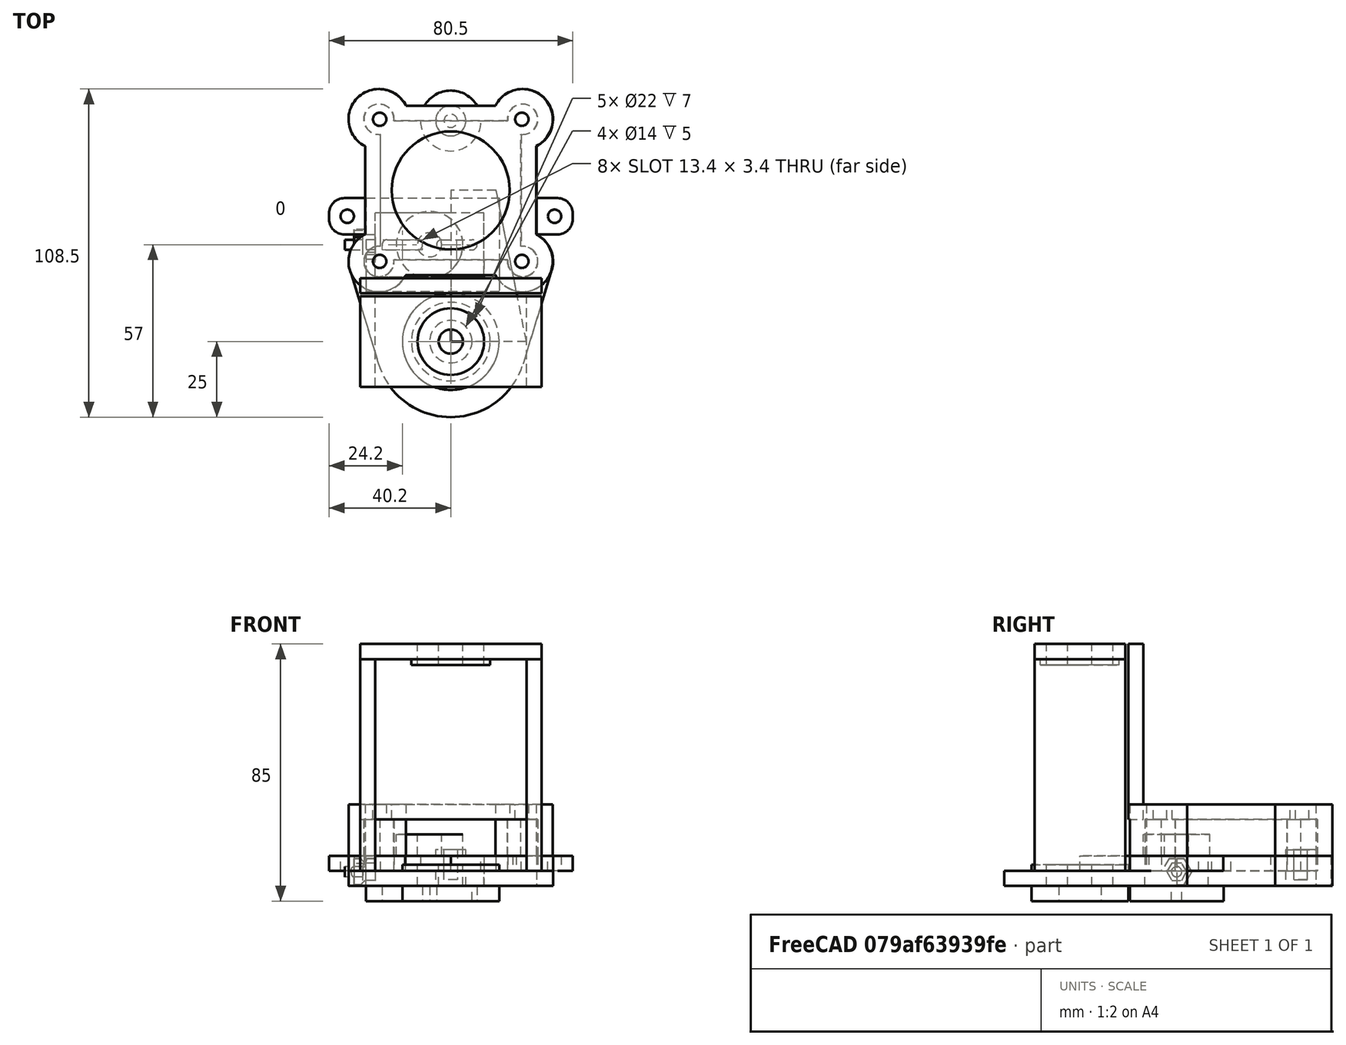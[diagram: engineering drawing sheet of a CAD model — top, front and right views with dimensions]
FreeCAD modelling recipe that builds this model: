
FCSTD DOCUMENT  (FreeCAD 0.16R6700 (Git))
Label: drive_full
License: All rights reserved
LicenseURL: http://en.wikipedia.org/wiki/All_rights_reserved
objects: Sketcher::SketchObject×23, PartDesign::Pocket×12, Part::Cylinder×8, PartDesign::Pad×8, Part::MultiFuse×5, Part::Cut×4, Part::Box×4, Mesh::Feature×3, Part::Extrusion×3, Part::Thickness×3, App::DocumentObjectGroup×1
note: 90 computed .brp shape members not serialized (recipe doc carries the construction recipe); baked Part::Feature solids carry a one-line shape summary decoded from their .brp

FEATURE [Mesh::Feature] pulley_full
  Placement = pos=(0,0,-3) rot=(0,0,1;0rad)
FEATURE [Part::Cylinder] Cylinder
  Angle = 360
  Height = 7
  Radius = 11
FEATURE [Part::Cylinder] Cylinder001
  Angle = 360
  Height = 7
  Radius = 4
FEATURE [Part::Cut] Cut  label="608"
  Base = -> Cylinder
  Placement = pos=(0,0,61) rot=(0,0,1;0rad)
  Tool = -> Cylinder001
FEATURE [Part::Cylinder] Cylinder002
  Angle = 360
  Height = 7
  Radius = 11
FEATURE [Part::Cylinder] Cylinder003
  Angle = 360
  Height = 7
  Radius = 4
FEATURE [Part::Cut] Cut001  label="608-1"
  Base = -> Cylinder002
  Placement = pos=(0,0,-12) rot=(0,0,1;0rad)
  Tool = -> Cylinder003
FEATURE [Mesh::Feature] nema23_76  label="nema23-76"
  Placement = pos=(0,50,14) rot=(0,0,1;0rad)
FEATURE [Part::Cylinder] Cylinder004
  Angle = 360
  Height = 7
  Radius = 11
FEATURE [Part::Cylinder] Cylinder005
  Angle = 360
  Height = 7
  Radius = 4
FEATURE [Part::Cut] Cut002  label="608-3"
  Base = -> Cylinder004
  Placement = pos=(-7,32,-2) rot=(0,0,1;0rad)
  Tool = -> Cylinder005
FEATURE [Part::Box] Box001  label="motor_wall"
  Height = 58
  Length = 60
  Placement = pos=(-30,16,10) rot=(0,0,1;0rad)
  Width = 5
FEATURE [Part::Box] Box002  label="rear_bearing_wall"
  Height = 5
  Length = 60
  Placement = pos=(-30,-15,66) rot=(0,0,1;0rad)
  Width = 30
FEATURE [Part::Cylinder] Cylinder012  label="rear_bearing_support"
  Angle = 360
  Height = 7
  Placement = pos=(0,0,64) rot=(0,0,1;0rad)
  Radius = 13
FEATURE [Part::Cylinder] Cylinder013  label="rear_bearing_hole"
  Angle = 360
  Height = 7
  Placement = pos=(0,0,64) rot=(0,0,1;0rad)
  Radius = 11
FEATURE [Part::MultiFuse] Fusion
  Shapes = -> [Cylinder012,Box002]
FEATURE [Part::Cut] Cut009  label="rear_pulley_wall"
  Base = -> Fusion
  Placement = pos=(0,0,-3) rot=(0,0,1;0rad)
  Tool = -> Cylinder013
FEATURE [Part::Box] Box004  label="side_wall"
  Height = 70
  Length = 5
  Placement = pos=(25,-15,-7) rot=(0,0,1;0rad)
  Width = 30
FEATURE [Part::Box] Box005  label="side_wall2"
  Height = 70
  Length = 5
  Placement = pos=(-30,-15,-7) rot=(0,0,1;0rad)
  Width = 30
FEATURE [App::DocumentObjectGroup] Group
FEATURE [Sketcher::SketchObject] Sketch002
  Placement = pos=(-30,-16,-12) rot=(0,0,1;0rad)
  sketch-geometry (7):
    g0: LineSegment StartX=2 StartY=63.5 StartZ=0 EndX=46 EndY=63.5 EndZ=0
    g1: LineSegment StartX=46 StartY=63.5 StartZ=0 EndX=46 EndY=32.5 EndZ=0
    g2: LineSegment StartX=46 StartY=32.5 StartZ=0 EndX=2 EndY=32.5 EndZ=0
    g3: LineSegment StartX=2 StartY=63.5 StartZ=0 EndX=2 EndY=32.5 EndZ=0
    g4: GeomPoint [constr] X=0 Y=52.9218 Z=0
    g5: GeomPoint [constr] X=2 Y=63.5 Z=0
    g6: GeomPoint [constr] X=8.31916 Y=32.5 Z=0
  constraints (15):
    c: Horizontal(g0)
    c: Vertical(g1)
    c: Horizontal(g2)
    c: Vertical(g3)
    c: Coincident(g0,g3)
    c: Coincident(g0,g1)
    c: Coincident(g1,g2)
    c: Coincident(g2,g3)
    c: DistanceY(g1,g1) = 31
    c: Distance(g2) = 44
    c: PointOnObject(g4,g-2)
    c: Coincident(g0,g5)
    c: DistanceX(g4,g5) = 2
    c: PointOnObject(g6,g2)
    c: DistanceY(g-1,g6) = 32.5
FEATURE [PartDesign::Pad] Pad  label="tuner_roof"
  Length = 5
  Length2 = 100
  Placement = pos=(-30,-16,-12) rot=(0,0,1;0rad)
  Reversed = true
  Sketch = -> Sketch002
  Type = 0
FEATURE [Sketcher::SketchObject] Sketch003
  ExternalGeometry = -> [Pad]
  Placement = pos=(-30,-16,-17) rot=(1,0,0;3.14159rad)
  Support = -> Pad [Face6]
  sketch-geometry (10):
    g0: ArcOfCircle CenterX=9 CenterY=-48 CenterZ=0 NormalX=0 NormalY=0 NormalZ=1 Radius=1.7 StartAngle=1.5708 EndAngle=4.71239
    g1: ArcOfCircle CenterX=19 CenterY=-48 CenterZ=0 NormalX=0 NormalY=0 NormalZ=1 Radius=1.7 StartAngle=4.71239 EndAngle=7.85398
    g2: LineSegment StartX=9 StartY=-49.7 StartZ=0 EndX=19 EndY=-49.7 EndZ=0
    g3: LineSegment StartX=9 StartY=-46.3 StartZ=0 EndX=19 EndY=-46.3 EndZ=0
    g4: ArcOfCircle CenterX=27 CenterY=-48 CenterZ=0 NormalX=0 NormalY=0 NormalZ=1 Radius=1.7 StartAngle=1.5708 EndAngle=4.71239
    g5: ArcOfCircle CenterX=37 CenterY=-48 CenterZ=0 NormalX=0 NormalY=0 NormalZ=1 Radius=1.7 StartAngle=4.71239 EndAngle=7.85398
    g6: LineSegment StartX=27 StartY=-49.7 StartZ=0 EndX=37 EndY=-49.7 EndZ=0
    g7: LineSegment StartX=27 StartY=-46.3 StartZ=0 EndX=37 EndY=-46.3 EndZ=0
    g8: GeomPoint [constr] X=6.41583 Y=-32.5 Z=0
    g9: GeomPoint [constr] X=0 Y=-49.7364 Z=0
  constraints (22):
    c: Tangent(g0,g3) = 1.5708
    c: Tangent(g0,g2) = -1.5708
    c: Tangent(g2,g1) = -1.5708
    c: Tangent(g3,g1) = 1.5708
    c: Horizontal(g2)
    c: Equal(g0,g1)
    c: Tangent(g4,g7) = 1.5708
    c: Tangent(g4,g6) = -1.5708
    c: Tangent(g6,g5) = -1.5708
    c: Tangent(g7,g5) = 1.5708
    c: Horizontal(g6)
    c: Equal(g4,g5)
    c: DistanceY(g0,g4) = 0
    c: Radius(g1) = 1.7
    c: Radius(g4) = 1.7
    c: PointOnObject(g8,g-3)
    c: DistanceY(g0,g8) = 15.5
    c: Distance(g1,g0) = 10
    c: Distance(g4,g5) = 10
    c: Distance(g5,g1) = 18
    c: PointOnObject(g9,g-2)
    c: DistanceX(g9,g0) = 9
FEATURE [PartDesign::Pocket] Pocket001  label="tune_bolts_cut"
  Length = 5
  Placement = pos=(-30,-16,-12) rot=(0,0,1;0rad)
  Sketch = -> Sketch003
  Type = 0
FEATURE [Mesh::Feature] bearing_holder
  Placement = pos=(-7,32,-12) rot=(0,0,1;3.14159rad)
FEATURE [Sketcher::SketchObject] Sketch006
  Placement = pos=(0,0,-2) rot=(0,0,1;0rad)
  sketch-geometry (21):
    g0: LineSegment StartX=-18.8251 StartY=27 StartZ=0 EndX=18.7251 EndY=27 EndZ=0
    g1: LineSegment StartX=23.2 StartY=31.4749 StartZ=0 EndX=23.2 EndY=68.5251 EndZ=0
    g2: LineSegment StartX=18.7251 StartY=73 StartZ=0 EndX=-18.8251 EndY=73 EndZ=0
    g3: LineSegment StartX=-23.3 StartY=68.5251 StartZ=0 EndX=-23.3 EndY=31.4749 EndZ=0
    g4: GeomPoint [constr] X=23.2 Y=67.9149 Z=0
    g5: GeomPoint [constr] X=18.0919 Y=73 Z=0
    g6: GeomPoint [constr] X=-23.3 Y=67.7035 Z=0
    g7: GeomPoint [constr] X=-23.3 Y=27 Z=0
    g8: GeomPoint [constr] X=23.2 Y=67.7619 Z=0
    g9: ArcOfCircle CenterX=-23.8 CenterY=26.5 CenterZ=0 NormalX=0 NormalY=0 NormalZ=1 Radius=5 StartAngle=1.47063 EndAngle=6.38335
    g10: GeomPoint [constr] X=-23.3 Y=27 Z=0
    g11: ArcOfCircle CenterX=23.7 CenterY=26.5 CenterZ=0 NormalX=0 NormalY=0 NormalZ=1 Radius=5 StartAngle=3.04143 EndAngle=7.95415
    g12: GeomPoint [constr] X=23.2 Y=27 Z=0
    g13: GeomPoint [constr] X=23.2 Y=27 Z=0
    g14: ArcOfCircle CenterX=23.7 CenterY=73.5 CenterZ=0 NormalX=0 NormalY=0 NormalZ=1 Radius=5 StartAngle=4.61222 EndAngle=9.52495
    g15: GeomPoint [constr] X=23.2 Y=66.2729 Z=0
    g16: ArcOfCircle CenterX=-23.8 CenterY=73.5 CenterZ=0 NormalX=0 NormalY=0 NormalZ=1 Radius=5 StartAngle=6.18302 EndAngle=11.0957
    g17: GeomPoint [constr] X=-9.4334 Y=27 Z=0
    g18: GeomPoint [constr] X=-8.84955 Y=0 Z=0
    g19: GeomPoint [constr] X=0 Y=23.7268 Z=0
    g20: GeomPoint [constr] X=23.2 Y=34.2071 Z=0
  constraints (43):
    c: Horizontal(g0)
    c: Horizontal(g2)
    c: Vertical(g1)
    c: Vertical(g3)
    c: PointOnObject(g4,g1)
    c: PointOnObject(g5,g2)
    c: PointOnObject(g6,g3)
    c: PointOnObject(g7,g0)
    c: DistanceY(g7,g5) = 46
    c: PointOnObject(g8,g1)
    c: DistanceX(g6,g8) = 46.5
    c: Radius(g9) = 5
    c: DistanceY(g9,g7) = 0.5
    c: PointOnObject(g10,g3)
    c: DistanceX(g9,g10) = 0.5
    c: Equal(g9,g11) = 5
    c: PointOnObject(g13,g1)
    c: DistanceY(g11,g12) = 0.5
    c: PointOnObject(g12,g0)
    c: DistanceX(g13,g11) = 0.5
    c: Coincident(g12,g13)
    c: Coincident(g7,g10)
    c: DistanceY(g5,g14) = 0.5
    c: PointOnObject(g15,g1)
    c: DistanceX(g15,g14) = 0.5
    c: DistanceX(g16,g6) = 0.5
    c: DistanceY(g5,g16) = 0.5
    c: Equal(g14,g16)
    c: Coincident(g2,g16)
    c: Coincident(g3,g16)
    c: Equal(g11,g14)
    c: Coincident(g1,g14)
    c: Coincident(g2,g14)
    c: Coincident(g11,g0)
    c: Coincident(g11,g1)
    c: Coincident(g0,g9)
    c: Coincident(g3,g9)
    c: PointOnObject(g17,g0)
    c: PointOnObject(g18,g-1)
    c: DistanceY(g18,g17) = 27
    c: PointOnObject(g19,g-2)
    c: PointOnObject(g20,g1)
    c: DistanceX(g19,g20) = 23.2
FEATURE [Part::Extrusion] Extrude
  Base = -> Sketch006
  Dir = (0,0,12)
  Solid = true
FEATURE [Part::Thickness] Thickness  label="curved_walls"
  Faces = -> Extrude [Face9]
  Intersection = false
  Join = 2
  Mode = 0
  SelfIntersection = false
  Value = 5
FEATURE [Sketcher::SketchObject] Sketch007
  Placement = pos=(0,0,15) rot=(0,0,1;0rad)
  Support = -> Thickness [Face19]
  sketch-geometry (7):
    g0: Circle CenterX=-23.5 CenterY=73.5 CenterZ=0 NormalX=0 NormalY=0 NormalZ=1 Radius=2.2
    g1: GeomPoint [constr] X=0 Y=49.9672 Z=0
    g2: GeomPoint [constr] X=-26.4919 Y=0 Z=0
    g3: Circle CenterX=-23.5 CenterY=26.5 CenterZ=0 NormalX=0 NormalY=0 NormalZ=1 Radius=2.2
    g4: Circle CenterX=23.5 CenterY=26.5 CenterZ=0 NormalX=0 NormalY=0 NormalZ=1 Radius=2.2
    g5: Circle CenterX=23.5 CenterY=73.5 CenterZ=0 NormalX=0 NormalY=0 NormalZ=1 Radius=2.2
    g6: Circle CenterX=0 CenterY=50 CenterZ=0 NormalX=0 NormalY=0 NormalZ=1 Radius=19.5
  constraints (17):
    c: Radius(g0) = 2.2
    c: PointOnObject(g1,g-2)
    c: DistanceX(g0,g1) = 23.5
    c: PointOnObject(g2,g-1)
    c: DistanceY(g2,g0) = 73.5
    c: Equal(g0,g3) = 2.2
    c: Equal(g3,g4)
    c: Equal(g5,g4)
    c: DistanceX(g3,g1) = 23.5
    c: DistanceX(g1,g5) = 23.5
    c: DistanceX(g1,g4) = 23.5
    c: DistanceY(g2,g5) = 73.5
    c: DistanceY(g2,g4) = 26.5
    c: DistanceY(g2,g3) = 26.5
    c: PointOnObject(g6,g-2)
    c: Radius(g6) = 19.5
    c: DistanceY(g2,g6) = 50
FEATURE [PartDesign::Pocket] Pocket003  label="bolt_holes"
  Length = 5
  Sketch = -> Sketch007
  Type = 0
FEATURE [Sketcher::SketchObject] Sketch008
  Placement = pos=(0,0,-7) rot=(0,0,1;0rad)
  sketch-geometry (21):
    g0: LineSegment StartX=-18.8251 StartY=27 StartZ=0 EndX=18.7251 EndY=27 EndZ=0
    g1: LineSegment StartX=23.2 StartY=31.4749 StartZ=0 EndX=23.2 EndY=68.5251 EndZ=0
    g2: LineSegment StartX=18.7251 StartY=73 StartZ=0 EndX=-18.8251 EndY=73 EndZ=0
    g3: LineSegment StartX=-23.3 StartY=68.5251 StartZ=0 EndX=-23.3 EndY=31.4749 EndZ=0
    g4: GeomPoint [constr] X=23.2 Y=67.9149 Z=0
    g5: GeomPoint [constr] X=18.0919 Y=73 Z=0
    g6: GeomPoint [constr] X=-23.3 Y=67.7035 Z=0
    g7: GeomPoint [constr] X=-23.3 Y=27 Z=0
    g8: GeomPoint [constr] X=23.2 Y=67.7619 Z=0
    g9: ArcOfCircle CenterX=-23.8 CenterY=26.5 CenterZ=0 NormalX=0 NormalY=0 NormalZ=1 Radius=5 StartAngle=1.47063 EndAngle=6.38335
    g10: GeomPoint [constr] X=-23.3 Y=27 Z=0
    g11: ArcOfCircle CenterX=23.7 CenterY=26.5 CenterZ=0 NormalX=0 NormalY=0 NormalZ=1 Radius=5 StartAngle=3.04143 EndAngle=7.95415
    g12: GeomPoint [constr] X=23.2 Y=27 Z=0
    g13: GeomPoint [constr] X=23.2 Y=27 Z=0
    g14: ArcOfCircle CenterX=23.7 CenterY=73.5 CenterZ=0 NormalX=0 NormalY=0 NormalZ=1 Radius=5 StartAngle=4.61222 EndAngle=9.52495
    g15: GeomPoint [constr] X=23.2 Y=66.2729 Z=0
    g16: ArcOfCircle CenterX=-23.8 CenterY=73.5 CenterZ=0 NormalX=0 NormalY=0 NormalZ=1 Radius=5 StartAngle=6.18302 EndAngle=11.0957
    g17: GeomPoint [constr] X=-9.4334 Y=27 Z=0
    g18: GeomPoint [constr] X=-8.84955 Y=0 Z=0
    g19: GeomPoint [constr] X=0 Y=23.7268 Z=0
    g20: GeomPoint [constr] X=23.2 Y=34.2071 Z=0
  constraints (43):
    c: Horizontal(g0)
    c: Horizontal(g2)
    c: Vertical(g1)
    c: Vertical(g3)
    c: PointOnObject(g4,g1)
    c: PointOnObject(g5,g2)
    c: PointOnObject(g6,g3)
    c: PointOnObject(g7,g0)
    c: DistanceY(g7,g5) = 46
    c: PointOnObject(g8,g1)
    c: DistanceX(g6,g8) = 46.5
    c: Radius(g9) = 5
    c: DistanceY(g9,g7) = 0.5
    c: PointOnObject(g10,g3)
    c: DistanceX(g9,g10) = 0.5
    c: Equal(g9,g11) = 5
    c: PointOnObject(g13,g1)
    c: DistanceY(g11,g12) = 0.5
    c: PointOnObject(g12,g0)
    c: DistanceX(g13,g11) = 0.5
    c: Coincident(g12,g13)
    c: Coincident(g7,g10)
    c: DistanceY(g5,g14) = 0.5
    c: PointOnObject(g15,g1)
    c: DistanceX(g15,g14) = 0.5
    c: DistanceX(g16,g6) = 0.5
    c: DistanceY(g5,g16) = 0.5
    c: Equal(g14,g16)
    c: Coincident(g2,g16)
    c: Coincident(g3,g16)
    c: Equal(g11,g14)
    c: Coincident(g1,g14)
    c: Coincident(g2,g14)
    c: Coincident(g11,g0)
    c: Coincident(g11,g1)
    c: Coincident(g0,g9)
    c: Coincident(g3,g9)
    c: PointOnObject(g17,g0)
    c: PointOnObject(g18,g-1)
    c: DistanceY(g18,g17) = 27
    c: PointOnObject(g19,g-2)
    c: PointOnObject(g20,g1)
    c: DistanceX(g19,g20) = 23.2
FEATURE [Part::Extrusion] Extrude001
  Base = -> Sketch008
  Dir = (0,0,-5)
  Solid = true
FEATURE [Part::Thickness] Thickness001  label="roof"
  Faces = -> Extrude001 [Face10]
  Intersection = false
  Join = 2
  Mode = 2
  Placement = pos=(0,0,-14) rot=(0,1,0;3.14159rad)
  SelfIntersection = false
  Value = 5
FEATURE [Sketcher::SketchObject] Sketch009
  ExternalGeometry = -> [Thickness001]
  Placement = pos=(0,0,-12) rot=(0,1,0;3.14159rad)
  Support = -> Thickness001 [Face19]
  sketch-geometry (6):
    g0: LineSegment StartX=-33.3619 StartY=23.5727 StartZ=0 EndX=-23.9049 EndY=-7.31832 EndZ=0
    g1: LineSegment StartX=33.2706 StartY=23.601 StartZ=0 EndX=23.9264 EndY=-7.24743 EndZ=0
    g2: LineSegment StartX=-23.8 StartY=26.5 StartZ=0 EndX=-33.3619 EndY=23.5727 EndZ=0
    g3: LineSegment StartX=23.7 StartY=26.5 StartZ=0 EndX=33.2706 EndY=23.601 EndZ=0
    g4: LineSegment StartX=-23.8 StartY=26.5 StartZ=0 EndX=23.7 EndY=26.5 EndZ=0
    g5: ArcOfCircle CenterX=0 CenterY=0 CenterZ=0 NormalX=0 NormalY=0 NormalZ=1 Radius=25 StartAngle=3.43868 EndAngle=5.98907
  constraints (14):
    c: PointOnObject(g0,g-3)
    c: Coincident(g2,g-3)
    c: Coincident(g2,g0)
    c: Perpendicular(g0,g2)
    c: Coincident(g3,g1)
    c: Perpendicular(g3,g1)
    c: Coincident(g4,g2)
    c: Tangent(g0,g5) = -1.5708
    c: Tangent(g1,g5) = 1.5708
    c: Radius(g5) = 25
    c: Coincident(g-1,g5)
    c: Coincident(g3,g4)
    c: Coincident(g3,g-4)
    c: PointOnObject(g1,g-4)
FEATURE [PartDesign::Pad] Pad001
  Length = 5
  Length2 = 100
  Placement = pos=(0,0,-14) rot=(0,1,0;3.14159rad)
  Reversed = true
  Sketch = -> Sketch009
  Type = 0
FEATURE [Part::MultiFuse] Fusion001  label="roof_full"
  Shapes = -> [Pad001,Thickness001]
FEATURE [Sketcher::SketchObject] Sketch010
  Placement = pos=(0,0,-12) rot=(1,0,0;3.14159rad)
  Support = -> Fusion001 [Face12]
  sketch-geometry (7):
    g0: LineSegment StartX=-25 StartY=-21.5 StartZ=0 EndX=11 EndY=-21.5 EndZ=0
    g1: LineSegment StartX=11 StartY=-21.5 StartZ=0 EndX=11 EndY=-42.5 EndZ=0
    g2: LineSegment StartX=11 StartY=-42.5 StartZ=0 EndX=-25 EndY=-42.5 EndZ=0
    g3: LineSegment StartX=-25 StartY=-21.5 StartZ=0 EndX=-25 EndY=-42.5 EndZ=0
    g4: GeomPoint [constr] X=0 Y=52.9218 Z=0
    g5: GeomPoint [constr] X=-25 Y=-21.5 Z=0
    g6: GeomPoint [constr] X=8.31916 Y=-42.5 Z=0
  constraints (15):
    c: Horizontal(g0)
    c: Vertical(g1)
    c: Horizontal(g2)
    c: Vertical(g3)
    c: Coincident(g0,g3)
    c: Coincident(g0,g1)
    c: Coincident(g1,g2)
    c: Coincident(g2,g3)
    c: DistanceY(g1,g1) = 21
    c: Distance(g2) = 36
    c: PointOnObject(g4,g-2)
    c: Coincident(g0,g5)
    c: DistanceX(g4,g5) = -25
    c: PointOnObject(g6,g2)
    c: DistanceY(g-1,g6) = -42.5
FEATURE [PartDesign::Pocket] Pocket
  Length = 10
  Sketch = -> Sketch010
  Type = 0
FEATURE [Sketcher::SketchObject] Sketch012
  Placement = pos=(0,0,-7) rot=(0,0,1;0rad)
  sketch-geometry (21):
    g0: LineSegment StartX=-18.8251 StartY=27 StartZ=0 EndX=18.7251 EndY=27 EndZ=0
    g1: LineSegment StartX=23.2 StartY=31.4749 StartZ=0 EndX=23.2 EndY=68.5251 EndZ=0
    g2: LineSegment StartX=18.7251 StartY=73 StartZ=0 EndX=-18.8251 EndY=73 EndZ=0
    g3: LineSegment StartX=-23.3 StartY=68.5251 StartZ=0 EndX=-23.3 EndY=31.4749 EndZ=0
    g4: GeomPoint [constr] X=23.2 Y=67.9149 Z=0
    g5: GeomPoint [constr] X=18.0919 Y=73 Z=0
    g6: GeomPoint [constr] X=-23.3 Y=67.7035 Z=0
    g7: GeomPoint [constr] X=-23.3 Y=27 Z=0
    g8: GeomPoint [constr] X=23.2 Y=67.7619 Z=0
    g9: ArcOfCircle CenterX=-23.8 CenterY=26.5 CenterZ=0 NormalX=0 NormalY=0 NormalZ=1 Radius=5 StartAngle=1.47063 EndAngle=6.38335
    g10: GeomPoint [constr] X=-23.3 Y=27 Z=0
    g11: ArcOfCircle CenterX=23.7 CenterY=26.5 CenterZ=0 NormalX=0 NormalY=0 NormalZ=1 Radius=5 StartAngle=3.04143 EndAngle=7.95415
    g12: GeomPoint [constr] X=23.2 Y=27 Z=0
    g13: GeomPoint [constr] X=23.2 Y=27 Z=0
    g14: ArcOfCircle CenterX=23.7 CenterY=73.5 CenterZ=0 NormalX=0 NormalY=0 NormalZ=1 Radius=5 StartAngle=4.61222 EndAngle=9.52495
    g15: GeomPoint [constr] X=23.2 Y=66.2729 Z=0
    g16: ArcOfCircle CenterX=-23.8 CenterY=73.5 CenterZ=0 NormalX=0 NormalY=0 NormalZ=1 Radius=5 StartAngle=6.18302 EndAngle=11.0957
    g17: GeomPoint [constr] X=-9.4334 Y=27 Z=0
    g18: GeomPoint [constr] X=-8.84955 Y=0 Z=0
    g19: GeomPoint [constr] X=0 Y=23.7268 Z=0
    g20: GeomPoint [constr] X=23.2 Y=34.2071 Z=0
  constraints (43):
    c: Horizontal(g0)
    c: Horizontal(g2)
    c: Vertical(g1)
    c: Vertical(g3)
    c: PointOnObject(g4,g1)
    c: PointOnObject(g5,g2)
    c: PointOnObject(g6,g3)
    c: PointOnObject(g7,g0)
    c: DistanceY(g7,g5) = 46
    c: PointOnObject(g8,g1)
    c: DistanceX(g6,g8) = 46.5
    c: Radius(g9) = 5
    c: DistanceY(g9,g7) = 0.5
    c: PointOnObject(g10,g3)
    c: DistanceX(g9,g10) = 0.5
    c: Equal(g9,g11) = 5
    c: PointOnObject(g13,g1)
    c: DistanceY(g11,g12) = 0.5
    c: PointOnObject(g12,g0)
    c: DistanceX(g13,g11) = 0.5
    c: Coincident(g12,g13)
    c: Coincident(g7,g10)
    c: DistanceY(g5,g14) = 0.5
    c: PointOnObject(g15,g1)
    c: DistanceX(g15,g14) = 0.5
    c: DistanceX(g16,g6) = 0.5
    c: DistanceY(g5,g16) = 0.5
    c: Equal(g14,g16)
    c: Coincident(g2,g16)
    c: Coincident(g3,g16)
    c: Equal(g11,g14)
    c: Coincident(g1,g14)
    c: Coincident(g2,g14)
    c: Coincident(g11,g0)
    c: Coincident(g11,g1)
    c: Coincident(g0,g9)
    c: Coincident(g3,g9)
    c: PointOnObject(g17,g0)
    c: PointOnObject(g18,g-1)
    c: DistanceY(g18,g17) = 27
    c: PointOnObject(g19,g-2)
    c: PointOnObject(g20,g1)
    c: DistanceX(g19,g20) = 23.2
FEATURE [Part::Extrusion] Extrude002
  Base = -> Sketch012
  Dir = (0,0,-5)
  Solid = true
FEATURE [Part::Thickness] Thickness002  label="roof001"
  Faces = -> Extrude002 [Face10]
  Intersection = false
  Join = 2
  Mode = 2
  Placement = pos=(0,0,-14) rot=(0,1,0;3.14159rad)
  SelfIntersection = false
  Value = 5
FEATURE [Sketcher::SketchObject] Sketch013
  ExternalGeometry = -> [Thickness002]
  Placement = pos=(0,0,-12) rot=(0,1,0;3.14159rad)
  Support = -> Thickness002 [Face19]
  sketch-geometry (6):
    g0: LineSegment StartX=-33.3619 StartY=23.5727 StartZ=0 EndX=-23.9049 EndY=-7.31832 EndZ=0
    g1: LineSegment StartX=33.2706 StartY=23.601 StartZ=0 EndX=23.9264 EndY=-7.24743 EndZ=0
    g2: LineSegment StartX=-23.8 StartY=26.5 StartZ=0 EndX=-33.3619 EndY=23.5727 EndZ=0
    g3: LineSegment StartX=23.7 StartY=26.5 StartZ=0 EndX=33.2706 EndY=23.601 EndZ=0
    g4: LineSegment StartX=-23.8 StartY=26.5 StartZ=0 EndX=23.7 EndY=26.5 EndZ=0
    g5: ArcOfCircle CenterX=0 CenterY=0 CenterZ=0 NormalX=0 NormalY=0 NormalZ=1 Radius=25 StartAngle=3.43868 EndAngle=5.98907
  constraints (14):
    c: PointOnObject(g0,g-3)
    c: Coincident(g2,g-3)
    c: Coincident(g2,g0)
    c: Perpendicular(g0,g2)
    c: Coincident(g3,g1)
    c: Perpendicular(g3,g1)
    c: Coincident(g4,g2)
    c: Tangent(g0,g5) = -1.5708
    c: Tangent(g1,g5) = 1.5708
    c: Radius(g5) = 25
    c: Coincident(g-1,g5)
    c: Coincident(g3,g4)
    c: Coincident(g3,g-4)
    c: PointOnObject(g1,g-4)
FEATURE [PartDesign::Pad] Pad002
  Length = 5
  Length2 = 100
  Placement = pos=(0,0,-14) rot=(0,1,0;3.14159rad)
  Reversed = true
  Sketch = -> Sketch013
  Type = 0
FEATURE [Part::MultiFuse] Fusion002  label="roof_full001"
  Shapes = -> [Pad002,Thickness002]
FEATURE [Sketcher::SketchObject] Sketch014
  Placement = pos=(0,0,-12) rot=(1,0,0;3.14159rad)
  Support = -> Fusion002 [Face12]
  sketch-geometry (7):
    g0: LineSegment StartX=-25 StartY=-21.5 StartZ=0 EndX=11 EndY=-21.5 EndZ=0
    g1: LineSegment StartX=11 StartY=-21.5 StartZ=0 EndX=11 EndY=-42.5 EndZ=0
    g2: LineSegment StartX=11 StartY=-42.5 StartZ=0 EndX=-25 EndY=-42.5 EndZ=0
    g3: LineSegment StartX=-25 StartY=-21.5 StartZ=0 EndX=-25 EndY=-42.5 EndZ=0
    g4: GeomPoint [constr] X=0 Y=52.9218 Z=0
    g5: GeomPoint [constr] X=-25 Y=-21.5 Z=0
    g6: GeomPoint [constr] X=8.31916 Y=-42.5 Z=0
  constraints (15):
    c: Horizontal(g0)
    c: Vertical(g1)
    c: Horizontal(g2)
    c: Vertical(g3)
    c: Coincident(g0,g3)
    c: Coincident(g0,g1)
    c: Coincident(g1,g2)
    c: Coincident(g2,g3)
    c: DistanceY(g1,g1) = 21
    c: Distance(g2) = 36
    c: PointOnObject(g4,g-2)
    c: Coincident(g0,g5)
    c: DistanceX(g4,g5) = -25
    c: PointOnObject(g6,g2)
    c: DistanceY(g-1,g6) = -42.5
FEATURE [PartDesign::Pocket] Pocket006  label="roof_w_tune_cut"
  Length = 10
  Sketch = -> Sketch014
  Type = 0
FEATURE [Sketcher::SketchObject] Sketch015
  Placement = pos=(0,0,-7) rot=(0,0,1;0rad)
  Support = -> Pocket006 [Face18]
  sketch-geometry (4):
    g0: LineSegment StartX=25 StartY=0 StartZ=0 EndX=15 EndY=50 EndZ=0
    g1: LineSegment StartX=15 StartY=50 StartZ=0 EndX=0 EndY=50 EndZ=0
    g2: LineSegment StartX=0 StartY=50 StartZ=0 EndX=0 EndY=0 EndZ=0
    g3: LineSegment StartX=25 StartY=0 StartZ=0 EndX=0 EndY=0 EndZ=0
  constraints (11):
    c: Coincident(g1,g0)
    c: Horizontal(g1)
    c: Coincident(g2,g-1)
    c: Coincident(g3,g0)
    c: Coincident(g3,g-1)
    c: Horizontal(g3)
    c: Coincident(g1,g2)
    c: Vertical(g2)
    c: Distance(g2) = 50
    c: Distance(g1) = 15
    c: Distance(g3) = 25
FEATURE [PartDesign::Pocket] Pocket007  label="belt_cutout001"
  Length = 5
  Reversed = true
  Sketch = -> Sketch015
  Type = 0
FEATURE [Sketcher::SketchObject] Sketch016
  Placement = pos=(-25,0,0) rot=(0.57735,0.57735,0.57735;2.0944rad)
  Support = -> Pocket007 [Face21]
  sketch-geometry (10):
    g0: LineSegment StartX=34.5115 StartY=-11.65 StartZ=0 EndX=37.0229 EndY=-7.3 EndZ=0
    g1: LineSegment StartX=37.0229 StartY=-7.3 StartZ=0 EndX=34.5115 EndY=-2.95 EndZ=0
    g2: LineSegment StartX=34.5115 StartY=-2.95 StartZ=0 EndX=29.4885 EndY=-2.95 EndZ=0
    g3: LineSegment StartX=29.4885 StartY=-2.95 StartZ=0 EndX=26.9771 EndY=-7.3 EndZ=0
    g4: LineSegment StartX=26.9771 StartY=-7.3 StartZ=0 EndX=29.4885 EndY=-11.65 EndZ=0
    g5: LineSegment StartX=29.4885 StartY=-11.65 StartZ=0 EndX=34.5115 EndY=-11.65 EndZ=0
    g6: Circle [constr] CenterX=32 CenterY=-7.3 CenterZ=0 NormalX=0 NormalY=0 NormalZ=1 Radius=5.02295
    g7: GeomPoint [constr] X=29.4885 Y=-2.95 Z=0
    g8: GeomPoint [constr] X=29.4885 Y=-11.65 Z=0
    g9: LineSegment [constr] StartX=26.9771 StartY=-7.3 StartZ=0 EndX=37.0229 EndY=-7.3 EndZ=0
  constraints (23):
    c: Coincident(g0,g1)
    c: Coincident(g1,g2)
    c: Coincident(g2,g3)
    c: Coincident(g3,g4)
    c: Coincident(g4,g5)
    c: Coincident(g5,g0)
    c: Equal(g0, g1-g5) x5
    c: PointOnObject(g0,g6)
    c: PointOnObject(g1,g6)
    c: PointOnObject(g2,g6)
    c: PointOnObject(g3,g6)
    c: PointOnObject(g4,g6)
    c: PointOnObject(g5,g6)
    c: PointOnObject(g8,g5)
    c: PointOnObject(g7,g2)
    c: DistanceY(g8,g7) = 8.7
    c: Coincident(g9,g3)
    c: Horizontal(g9)
    c: Coincident(g9,g0)
    c: Coincident(g7,g2)
    c: Coincident(g8,g4)
    c: DistanceY(g6,g-1) = 7.3
    c: DistanceX(g-1,g6) = 32
FEATURE [PartDesign::Pad] Pad003
  Length = 7
  Length2 = 100
  Reversed = true
  Sketch = -> Sketch016
  Type = 0
FEATURE [Part::MultiFuse] Fusion003  label="roof_w_tune_nc"
  Shapes = -> [Pad003,Pocket006]
FEATURE [Sketcher::SketchObject] Sketch011
  Placement = pos=(-25,0,0) rot=(0.57735,0.57735,0.57735;2.0944rad)
  Support = -> Fusion003 [Face20]
  sketch-geometry (10):
    g0: LineSegment StartX=33.6454 StartY=-10.15 StartZ=0 EndX=35.2909 EndY=-7.3 EndZ=0
    g1: LineSegment StartX=35.2909 StartY=-7.3 StartZ=0 EndX=33.6454 EndY=-4.45 EndZ=0
    g2: LineSegment StartX=33.6454 StartY=-4.45 StartZ=0 EndX=30.3546 EndY=-4.45 EndZ=0
    g3: LineSegment StartX=30.3546 StartY=-4.45 StartZ=0 EndX=28.7091 EndY=-7.3 EndZ=0
    g4: LineSegment StartX=28.7091 StartY=-7.3 StartZ=0 EndX=30.3546 EndY=-10.15 EndZ=0
    g5: LineSegment StartX=30.3546 StartY=-10.15 StartZ=0 EndX=33.6454 EndY=-10.15 EndZ=0
    g6: Circle [constr] CenterX=32 CenterY=-7.3 CenterZ=0 NormalX=0 NormalY=0 NormalZ=1 Radius=3.2909
    g7: GeomPoint [constr] X=30.3546 Y=-4.45 Z=0
    g8: GeomPoint [constr] X=30.3546 Y=-10.15 Z=0
    g9: LineSegment [constr] StartX=28.7091 StartY=-7.3 StartZ=0 EndX=35.2909 EndY=-7.3 EndZ=0
  constraints (23):
    c: Coincident(g0,g1)
    c: Coincident(g1,g2)
    c: Coincident(g2,g3)
    c: Coincident(g3,g4)
    c: Coincident(g4,g5)
    c: Coincident(g5,g0)
    c: Equal(g0, g1-g5) x5
    c: PointOnObject(g0,g6)
    c: PointOnObject(g1,g6)
    c: PointOnObject(g2,g6)
    c: PointOnObject(g3,g6)
    c: PointOnObject(g4,g6)
    c: PointOnObject(g5,g6)
    c: PointOnObject(g8,g5)
    c: PointOnObject(g7,g2)
    c: DistanceY(g8,g7) = 5.7
    c: Coincident(g9,g3)
    c: Horizontal(g9)
    c: Coincident(g9,g0)
    c: Coincident(g7,g2)
    c: Coincident(g8,g4)
    c: DistanceY(g6,g-1) = 7.3
    c: DistanceX(g-1,g6) = 32
FEATURE [PartDesign::Pocket] Pocket005
  Length = 4
  Sketch = -> Sketch011
  Type = 0
FEATURE [Sketcher::SketchObject] Sketch017
  Placement = pos=(-32,0,0) rot=(0.57735,-0.57735,-0.57735;2.0944rad)
  Support = -> Pocket005 [Face25]
  sketch-geometry (1):
    g0: Circle CenterX=-32 CenterY=-7.3 CenterZ=0 NormalX=0 NormalY=0 NormalZ=1 Radius=1.7
  constraints (3):
    c: Radius(g0) = 1.7
    c: DistanceX(g0,g-1) = 32
    c: DistanceY(g0,g-1) = 7.3
FEATURE [PartDesign::Pocket] Pocket008
  Length = 6
  Midplane = true
  Sketch = -> Sketch017
  Type = 0
FEATURE [Sketcher::SketchObject] Sketch  label="belt_cut"
  Placement = pos=(0,0,-7) rot=(0,0,1;0rad)
  Support = -> Pocket008 [Face4]
  sketch-geometry (4):
    g0: LineSegment StartX=25 StartY=0 StartZ=0 EndX=15 EndY=50 EndZ=0
    g1: LineSegment StartX=15 StartY=50 StartZ=0 EndX=0 EndY=50 EndZ=0
    g2: LineSegment StartX=0 StartY=50 StartZ=0 EndX=0 EndY=0 EndZ=0
    g3: LineSegment StartX=25 StartY=0 StartZ=0 EndX=0 EndY=0 EndZ=0
  constraints (11):
    c: Coincident(g1,g0)
    c: Horizontal(g1)
    c: Coincident(g2,g-1)
    c: Coincident(g3,g0)
    c: Coincident(g3,g-1)
    c: Horizontal(g3)
    c: Coincident(g1,g2)
    c: Vertical(g2)
    c: Distance(g2) = 50
    c: Distance(g1) = 15
    c: Distance(g3) = 25
FEATURE [PartDesign::Pocket] Pocket009
  Length = 5
  Reversed = true
  Sketch = -> Sketch
  Type = 0
FEATURE [Sketcher::SketchObject] Sketch018
  Placement = pos=(0,0,-12) rot=(1,0,0;3.14159rad)
  Support = -> Pocket009 [Face3]
  sketch-geometry (1):
    g0: Circle CenterX=0 CenterY=0 CenterZ=0 NormalX=0 NormalY=0 NormalZ=1 Radius=16
  constraints (2):
    c: Coincident(g0,g-1)
    c: Radius(g0) = 16
FEATURE [PartDesign::Pad] Pad004  label="bearing_t_holder"
  Length = 5
  Length2 = 7
  Sketch = -> Sketch018
  Type = 4
FEATURE [Sketcher::SketchObject] Sketch019  label="t_bearing_cut"
  Placement = pos=(0,0,-5) rot=(0,0,1;0rad)
  Support = -> Pad004 [Face24]
  sketch-geometry (1):
    g0: Circle CenterX=0 CenterY=0 CenterZ=0 NormalX=0 NormalY=0 NormalZ=1 Radius=11
  constraints (2):
    c: Coincident(g0,g-1)
    c: Radius(g0) = 11
FEATURE [PartDesign::Pocket] Pocket010
  Length = 7
  Sketch = -> Sketch019
  Type = 0
FEATURE [Sketcher::SketchObject] Sketch020
  Placement = pos=(0,0,-17) rot=(1,0,0;3.14159rad)
  Support = -> Pocket010 [Face23]
  sketch-geometry (1):
    g0: Circle CenterX=0 CenterY=0 CenterZ=0 NormalX=0 NormalY=0 NormalZ=1 Radius=7
  constraints (2):
    c: Coincident(g0,g-1)
    c: Radius(g0) = 7
FEATURE [PartDesign::Pocket] Pocket011  label="roof002"
  Length = 5
  Sketch = -> Sketch020
  Type = 0
FEATURE [Part::MultiFuse] Fusion004  label="roof003"
  Shapes = -> [Pocket001,Pocket011]
FEATURE [Sketcher::SketchObject] Sketch021
  ExternalGeometry = -> [Fusion004]
  Placement = pos=(0,0,-7) rot=(0,0,1;0rad)
  Support = -> Fusion004 [Face49]
  sketch-geometry (2):
    g0: Circle CenterX=0 CenterY=73 CenterZ=0 NormalX=0 NormalY=0 NormalZ=1 Radius=10
    g1: GeomPoint [constr] X=0 Y=73 Z=0
  constraints (5):
    c: PointOnObject(g0,g-2)
    c: Radius(g0) = 10
    c: PointOnObject(g1,g-3)
    c: DistanceY(g0,g1) = 0
    c: PointOnObject(g1,g-2)
FEATURE [PartDesign::Pad] Pad005
  Length = 5
  Length2 = 5
  Sketch = -> Sketch021
  Type = 4
FEATURE [Sketcher::SketchObject] Sketch022
  ExternalGeometry = -> [Pad005]
  Placement = pos=(0,0,-2) rot=(0,0,1;0rad)
  Support = -> Pad005 [Face81]
  sketch-geometry (1):
    g0: Circle CenterX=0 CenterY=73 CenterZ=0 NormalX=0 NormalY=0 NormalZ=1 Radius=5
  constraints (2):
    c: Coincident(g0,g-3)
    c: Radius(g0) = 5
FEATURE [PartDesign::Pad] Pad006
  Length = 2
  Length2 = 100
  Sketch = -> Sketch022
  Type = 0
FEATURE [Sketcher::SketchObject] Sketch023
  ExternalGeometry = -> [Pad006]
  Placement = pos=(0,0,-12) rot=(1,0,0;3.14159rad)
  Support = -> Pad006 [Face25]
  sketch-geometry (1):
    g0: Circle CenterX=0 CenterY=-73 CenterZ=0 NormalX=0 NormalY=0 NormalZ=1 Radius=5
  constraints (2):
    c: Coincident(g0,g-3)
    c: Radius(g0) = 5
FEATURE [PartDesign::Pocket] Pocket012
  Length = 5
  Sketch = -> Sketch023
  Type = 0
FEATURE [Sketcher::SketchObject] Sketch024
  ExternalGeometry = -> [Pocket012]
  Support = -> Pocket012 [Face88]
  sketch-geometry (1):
    g0: Circle CenterX=0 CenterY=73 CenterZ=0 NormalX=0 NormalY=0 NormalZ=1 Radius=2.2
  constraints (2):
    c: Coincident(g0,g-3)
    c: Radius(g0) = 2.2
FEATURE [PartDesign::Pocket] Pocket013
  Length = 10
  Sketch = -> Sketch024
  Type = 0
FEATURE [Sketcher::SketchObject] Sketch025
  ExternalGeometry = -> [Pocket013]
  Placement = pos=(0,0,-2) rot=(0,0,1;0rad)
  Support = -> Pocket013 [Face44]
  sketch-geometry (18):
    g0: LineSegment StartX=-28.2 StartY=35.4303 StartZ=0 EndX=-35.2 EndY=35.4303 EndZ=0
    g1: LineSegment StartX=-40.2 StartY=40.4303 StartZ=0 EndX=-40.2 EndY=42.4303 EndZ=0
    g2: LineSegment StartX=-35.2 StartY=47.4303 StartZ=0 EndX=-28.2 EndY=47.4303 EndZ=0
    g3: LineSegment StartX=-28.2 StartY=47.4303 StartZ=0 EndX=-28.2 EndY=35.4303 EndZ=0
    g4: LineSegment StartX=28.3 StartY=35.4303 StartZ=0 EndX=35.3 EndY=35.4303 EndZ=0
    g5: LineSegment StartX=40.3 StartY=40.4303 StartZ=0 EndX=40.3 EndY=42.4303 EndZ=0
    g6: LineSegment StartX=35.3 StartY=47.4303 StartZ=0 EndX=28.3 EndY=47.4303 EndZ=0
    g7: LineSegment StartX=28.3 StartY=47.4303 StartZ=0 EndX=28.3 EndY=35.4303 EndZ=0
    g8: GeomPoint [constr] X=-40.2 Y=42.2516 Z=0
    g9: ArcOfCircle CenterX=-35.2 CenterY=42.4303 CenterZ=0 NormalX=0 NormalY=0 NormalZ=1 Radius=5 StartAngle=1.5708 EndAngle=3.14159
    g10: ArcOfCircle CenterX=-35.2 CenterY=40.4303 CenterZ=0 NormalX=0 NormalY=0 NormalZ=1 Radius=5 StartAngle=3.14159 EndAngle=4.71239
    g11: GeomPoint [constr] X=-34.2 Y=41.4303 Z=0
    g12: Circle CenterX=-34.2 CenterY=41.4303 CenterZ=0 NormalX=0 NormalY=0 NormalZ=1 Radius=2.2
    g13: GeomPoint [constr] X=40.3 Y=41.4745 Z=0
    g14: ArcOfCircle CenterX=35.3 CenterY=42.4303 CenterZ=0 NormalX=0 NormalY=0 NormalZ=1 Radius=5 StartAngle=0 EndAngle=1.5708
    g15: ArcOfCircle CenterX=35.3 CenterY=40.4303 CenterZ=0 NormalX=0 NormalY=0 NormalZ=1 Radius=5 StartAngle=4.71239 EndAngle=6.28319
    g16: GeomPoint [constr] X=34.3 Y=41.4303 Z=0
    g17: Circle CenterX=34.3 CenterY=41.4303 CenterZ=0 NormalX=0 NormalY=0 NormalZ=1 Radius=2.2
  constraints (40):
    c: Coincident(g2,g3)
    c: Coincident(g3,g0)
    c: Horizontal(g0)
    c: Horizontal(g2)
    c: Vertical(g1)
    c: Vertical(g3)
    c: Coincident(g0,g-4)
    c: Coincident(g6,g7)
    c: Coincident(g7,g4)
    c: Horizontal(g4)
    c: Horizontal(g6)
    c: Vertical(g5)
    c: Vertical(g7)
    c: Coincident(g4,g-3)
    c: PointOnObject(g8,g1)
    c: DistanceX(g8,g0) = 12
    c: DistanceY(g0,g2) = 12
    c: Tangent(g2,g9) = 1.5708
    c: Tangent(g1,g9) = 1.5708
    c: Tangent(g1,g10) = 1.5708
    c: Tangent(g0,g10) = 1.5708
    c: Radius(g10) = 5
    c: Radius(g9) = 5
    c: DistanceY(g11,g2) = 6
    c: DistanceX(g1,g11) = 6
    c: Coincident(g12,g11)
    c: Radius(g12) = 2.2
    c: PointOnObject(g13,g5)
    c: DistanceX(g4,g13) = 12
    c: DistanceY(g4,g6) = 12
    c: Tangent(g6,g14) = -1.5708
    c: Tangent(g5,g14) = -1.5708
    c: Tangent(g5,g15) = -1.5708
    c: Tangent(g4,g15) = -1.5708
    c: Radius(g15) = 5
    c: Equal(g15,g14)
    c: DistanceX(g4,g16) = 6
    c: DistanceY(g4,g16) = 6
    c: Coincident(g17,g16)
    c: Radius(g17) = 2.2
FEATURE [PartDesign::Pad] Pad007
  Length = 5
  Length2 = 100
  Reversed = true
  Sketch = -> Sketch025
  Type = 0
